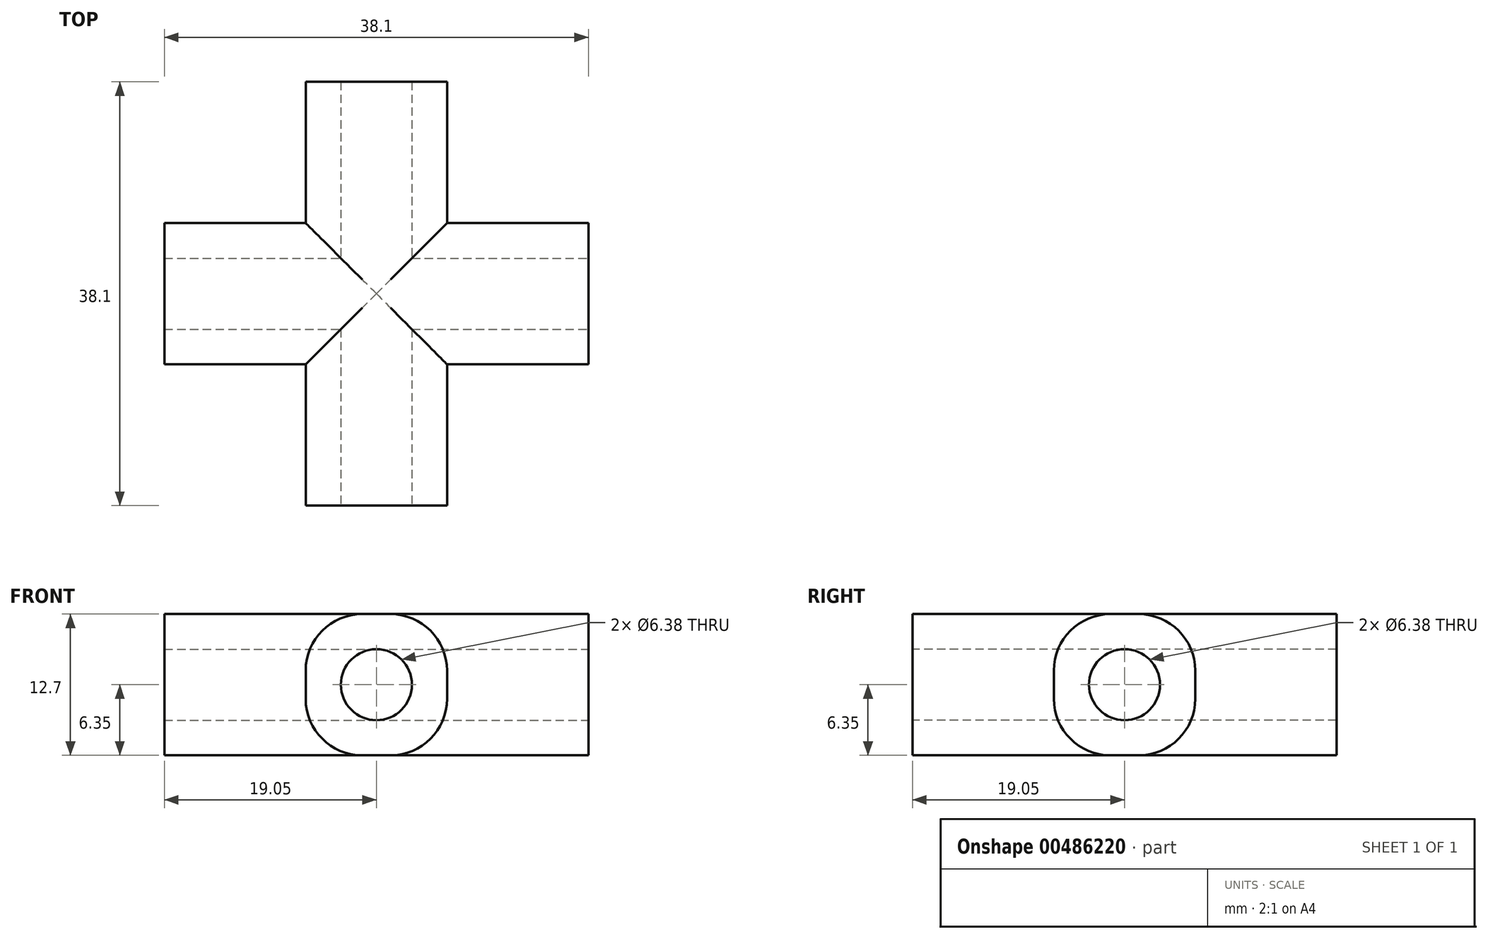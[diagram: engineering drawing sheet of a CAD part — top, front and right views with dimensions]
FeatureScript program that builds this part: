
annotation { "Feature Type Name" : "Feature", "Feature Type Description" : "" }
export const myFeature = defineFeature(function(context is Context, id is Id, definition is map)
    precondition{}
    {
        {
            var Q0;
            Q0=qCreatedBy(makeId("Top.planeOp"),FACE);
            var sketch = newSketch(context, id + "F0", { "sketchPlane" : qUnion([Q0])});
            skLineSegment(sketch, "E0.bottom", {"start": v(6.35, 19.05) * mm, "end": v(-6.35, 19.05) * mm});
            skLineSegment(sketch, "E0.top", {"start": v(6.35, -19.05) * mm, "end": v(-6.35, -19.05) * mm});
            skLineSegment(sketch, "E0.left", {"start": v(6.35, 19.05) * mm, "end": v(6.35, -19.05) * mm});
            skLineSegment(sketch, "E0.right", {"start": v(-6.35, 19.05) * mm, "end": v(-6.35, -19.05) * mm});
            skPoint(sketch, "E0.middle", {"position": v(0, 0) * mm});
            skLineSegment(sketch, "E1.bottom", {"start": v(19.05, 6.35) * mm, "end": v(-19.05, 6.35) * mm});
            skLineSegment(sketch, "E1.top", {"start": v(19.05, -6.35) * mm, "end": v(-19.05, -6.35) * mm});
            skLineSegment(sketch, "E1.left", {"start": v(19.05, 6.35) * mm, "end": v(19.05, -6.35) * mm});
            skLineSegment(sketch, "E1.right", {"start": v(-19.05, 6.35) * mm, "end": v(-19.05, -6.35) * mm});
            skSolve(sketch);
        }
        {
            var Q0;
            Q0 = qSketchRegion(id + "F0", true);
            extrude(context, id + "F1", {"entities" : qUnion([Q0]), "depth" : 12.7 * mm, "offsetDistance" : 25.4 * mm});
        }
        {
            var Q0;
            Q0=makeQuery(id+"F1.opExtrude","SWEPT_FACE",FACE,{"disambiguationData":[OSD([sQuery(id+"F0.wireOp",EDGE,"E1.left")])]});
            var sketch = newSketch(context, id + "F2", { "sketchPlane" : qUnion([Q0])});
            skLineSegment(sketch, "E2", {"start": v(0, 12.7) * mm, "end": v(0, 0) * mm});
            skCircle(sketch, "E3", {"center": v(0, 6.35) * mm, "radius": 3.19 * mm});
            skSolve(sketch);
        }
        {
            var Q0;
            Q0=makeQuery(id+"F1.opExtrude","SWEPT_FACE",FACE,{"disambiguationData":[OSD([sQuery(id+"F0.wireOp",EDGE,"E0.top")])]});
            var sketch = newSketch(context, id + "F3", { "sketchPlane" : qUnion([Q0])});
            skLineSegment(sketch, "E4", {"start": v(0, 12.7) * mm, "end": v(0, 0) * mm, "construction": true});
            skCircle(sketch, "E5", {"center": v(0, 6.35) * mm, "radius": 3.19 * mm});
            skSolve(sketch);
        }
        {
            var Q0;
            {var subQ0=sQuery(id+"F2.wireOp",EDGE,"E3");var subQ1=sQuery(id+"F2.wireOp",EDGE,"E2");var subQ2=makeQuery(id+"F2.imprint","INTERSECT",VERTEX,{"disambiguationData":[OD(0.0)],"derivedFrom":[subQ1,subQ0]});Q0=makeQuery(id+"F2.imprint","IMPRINT",FACE,{"disambiguationData":[TD([[makeQuery(id+"F2.imprint","IMPRINT",EDGE,{"disambiguationData":[TD([[subQ2,-1.0]])],"derivedFrom":subQ1}),-1.0]])]});}
            var Q1;
            {var subQ0=sQuery(id+"F2.wireOp",EDGE,"E3");var subQ1=sQuery(id+"F2.wireOp",EDGE,"E2");var subQ2=makeQuery(id+"F2.imprint","INTERSECT",VERTEX,{"disambiguationData":[OD(0.0)],"derivedFrom":[subQ1,subQ0]});Q1=makeQuery(id+"F2.imprint","IMPRINT",FACE,{"disambiguationData":[TD([[makeQuery(id+"F2.imprint","IMPRINT",EDGE,{"disambiguationData":[TD([[subQ2,-1.0]])],"derivedFrom":subQ1}),1.0]])]});}
            extrude(context, id + "F4", {"entities" : qUnion([Q0, Q1]), "operationType" : NewBodyOperationType.REMOVE, "oppositeDirection" : true, "depth" : 50.8 * mm, "offsetDistance" : 25.4 * mm});
        }
        {
            var Q0;
            Q0=makeQuery(id+"F3.imprint","IMPRINT",FACE,{"disambiguationData":[TD([[makeQuery(id+"F3.imprint","IMPRINT",EDGE,{"derivedFrom":sQuery(id+"F3.wireOp",EDGE,"E5")}),1.0]])]});
            extrude(context, id + "F5", {"entities" : qUnion([Q0]), "operationType" : NewBodyOperationType.REMOVE, "oppositeDirection" : true, "depth" : 76.2 * mm, "offsetDistance" : 25.4 * mm});
        }
        {
            var Q0;
            {var subQ0=sQuery(id+"F0.wireOp",EDGE,"E0.right");Q0=makeQuery(id+"F1.opExtrude","CAP_EDGE",EDGE,{"disambiguationData":[OSD([subQ0]),TDD([makeQuery(id+"F0.imprint","IMPRINT",EDGE,{"disambiguationData":[TD([[makeQuery(id+"F0.imprint","INTERSECT",VERTEX,{"derivedFrom":[sQuery(id+"F0.wireOp",EDGE,"E0.top"),subQ0]}),1.0]])],"derivedFrom":subQ0})])],"isStart":true});}
            var Q1;
            {var subQ0=sQuery(id+"F0.wireOp",EDGE,"E0.left");Q1=makeQuery(id+"F1.opExtrude","CAP_EDGE",EDGE,{"disambiguationData":[OSD([subQ0]),TDD([makeQuery(id+"F0.imprint","IMPRINT",EDGE,{"disambiguationData":[TD([[makeQuery(id+"F0.imprint","INTERSECT",VERTEX,{"derivedFrom":[sQuery(id+"F0.wireOp",EDGE,"E0.top"),subQ0]}),1.0]])],"derivedFrom":subQ0})])],"isStart":true});}
            var Q2;
            {var subQ0=sQuery(id+"F0.wireOp",EDGE,"E1.top");Q2=makeQuery(id+"F1.opExtrude","CAP_EDGE",EDGE,{"disambiguationData":[OSD([subQ0]),TDD([makeQuery(id+"F0.imprint","IMPRINT",EDGE,{"disambiguationData":[TD([[makeQuery(id+"F0.imprint","INTERSECT",VERTEX,{"derivedFrom":[subQ0,sQuery(id+"F0.wireOp",EDGE,"E1.left")]}),-1.0]])],"derivedFrom":subQ0})])],"isStart":true});}
            var Q3;
            {var subQ0=sQuery(id+"F0.wireOp",EDGE,"E1.bottom");Q3=makeQuery(id+"F1.opExtrude","CAP_EDGE",EDGE,{"disambiguationData":[OSD([subQ0]),TDD([makeQuery(id+"F0.imprint","IMPRINT",EDGE,{"disambiguationData":[TD([[makeQuery(id+"F0.imprint","INTERSECT",VERTEX,{"derivedFrom":[subQ0,sQuery(id+"F0.wireOp",EDGE,"E1.left")]}),-1.0]])],"derivedFrom":subQ0})])],"isStart":true});}
            var Q4;
            {var subQ0=sQuery(id+"F0.wireOp",EDGE,"E0.left");Q4=makeQuery(id+"F1.opExtrude","CAP_EDGE",EDGE,{"disambiguationData":[OSD([subQ0]),TDD([makeQuery(id+"F0.imprint","IMPRINT",EDGE,{"disambiguationData":[TD([[makeQuery(id+"F0.imprint","INTERSECT",VERTEX,{"derivedFrom":[sQuery(id+"F0.wireOp",EDGE,"E0.bottom"),subQ0]}),-1.0]])],"derivedFrom":subQ0})])],"isStart":true});}
            var Q5;
            {var subQ0=sQuery(id+"F0.wireOp",EDGE,"E0.right");Q5=makeQuery(id+"F1.opExtrude","CAP_EDGE",EDGE,{"disambiguationData":[OSD([subQ0]),TDD([makeQuery(id+"F0.imprint","IMPRINT",EDGE,{"disambiguationData":[TD([[makeQuery(id+"F0.imprint","INTERSECT",VERTEX,{"derivedFrom":[sQuery(id+"F0.wireOp",EDGE,"E0.bottom"),subQ0]}),-1.0]])],"derivedFrom":subQ0})])],"isStart":true});}
            var Q6;
            {var subQ0=sQuery(id+"F0.wireOp",EDGE,"E1.top");Q6=makeQuery(id+"F1.opExtrude","CAP_EDGE",EDGE,{"disambiguationData":[OSD([subQ0]),TDD([makeQuery(id+"F0.imprint","IMPRINT",EDGE,{"disambiguationData":[TD([[makeQuery(id+"F0.imprint","INTERSECT",VERTEX,{"derivedFrom":[subQ0,sQuery(id+"F0.wireOp",EDGE,"E1.right")]}),1.0]])],"derivedFrom":subQ0})])],"isStart":true});}
            var Q7;
            {var subQ0=sQuery(id+"F0.wireOp",EDGE,"E1.bottom");Q7=makeQuery(id+"F1.opExtrude","CAP_EDGE",EDGE,{"disambiguationData":[OSD([subQ0]),TDD([makeQuery(id+"F0.imprint","IMPRINT",EDGE,{"disambiguationData":[TD([[makeQuery(id+"F0.imprint","INTERSECT",VERTEX,{"derivedFrom":[subQ0,sQuery(id+"F0.wireOp",EDGE,"E1.right")]}),1.0]])],"derivedFrom":subQ0})])],"isStart":true});}
            var Q8;
            {var subQ0=sQuery(id+"F0.wireOp",EDGE,"E1.top");Q8=makeQuery(id+"F1.opExtrude","CAP_EDGE",EDGE,{"disambiguationData":[OSD([subQ0]),TDD([makeQuery(id+"F0.imprint","IMPRINT",EDGE,{"disambiguationData":[TD([[makeQuery(id+"F0.imprint","INTERSECT",VERTEX,{"derivedFrom":[subQ0,sQuery(id+"F0.wireOp",EDGE,"E1.right")]}),1.0]])],"derivedFrom":subQ0})])],"isStart":false});}
            var Q9;
            {var subQ0=sQuery(id+"F0.wireOp",EDGE,"E0.right");Q9=makeQuery(id+"F1.opExtrude","CAP_EDGE",EDGE,{"disambiguationData":[OSD([subQ0]),TDD([makeQuery(id+"F0.imprint","IMPRINT",EDGE,{"disambiguationData":[TD([[makeQuery(id+"F0.imprint","INTERSECT",VERTEX,{"derivedFrom":[sQuery(id+"F0.wireOp",EDGE,"E0.top"),subQ0]}),1.0]])],"derivedFrom":subQ0})])],"isStart":false});}
            var Q10;
            {var subQ0=sQuery(id+"F0.wireOp",EDGE,"E1.top");Q10=makeQuery(id+"F1.opExtrude","CAP_EDGE",EDGE,{"disambiguationData":[OSD([subQ0]),TDD([makeQuery(id+"F0.imprint","IMPRINT",EDGE,{"disambiguationData":[TD([[makeQuery(id+"F0.imprint","INTERSECT",VERTEX,{"derivedFrom":[subQ0,sQuery(id+"F0.wireOp",EDGE,"E1.left")]}),-1.0]])],"derivedFrom":subQ0})])],"isStart":false});}
            var Q11;
            {var subQ0=sQuery(id+"F0.wireOp",EDGE,"E1.bottom");Q11=makeQuery(id+"F1.opExtrude","CAP_EDGE",EDGE,{"disambiguationData":[OSD([subQ0]),TDD([makeQuery(id+"F0.imprint","IMPRINT",EDGE,{"disambiguationData":[TD([[makeQuery(id+"F0.imprint","INTERSECT",VERTEX,{"derivedFrom":[subQ0,sQuery(id+"F0.wireOp",EDGE,"E1.right")]}),1.0]])],"derivedFrom":subQ0})])],"isStart":false});}
            var Q12;
            {var subQ0=sQuery(id+"F0.wireOp",EDGE,"E0.right");Q12=makeQuery(id+"F1.opExtrude","CAP_EDGE",EDGE,{"disambiguationData":[OSD([subQ0]),TDD([makeQuery(id+"F0.imprint","IMPRINT",EDGE,{"disambiguationData":[TD([[makeQuery(id+"F0.imprint","INTERSECT",VERTEX,{"derivedFrom":[sQuery(id+"F0.wireOp",EDGE,"E0.bottom"),subQ0]}),-1.0]])],"derivedFrom":subQ0})])],"isStart":false});}
            var Q13;
            {var subQ0=sQuery(id+"F0.wireOp",EDGE,"E0.left");Q13=makeQuery(id+"F1.opExtrude","CAP_EDGE",EDGE,{"disambiguationData":[OSD([subQ0]),TDD([makeQuery(id+"F0.imprint","IMPRINT",EDGE,{"disambiguationData":[TD([[makeQuery(id+"F0.imprint","INTERSECT",VERTEX,{"derivedFrom":[sQuery(id+"F0.wireOp",EDGE,"E0.bottom"),subQ0]}),-1.0]])],"derivedFrom":subQ0})])],"isStart":false});}
            var Q14;
            {var subQ0=sQuery(id+"F0.wireOp",EDGE,"E0.left");Q14=makeQuery(id+"F1.opExtrude","CAP_EDGE",EDGE,{"disambiguationData":[OSD([subQ0]),TDD([makeQuery(id+"F0.imprint","IMPRINT",EDGE,{"disambiguationData":[TD([[makeQuery(id+"F0.imprint","INTERSECT",VERTEX,{"derivedFrom":[sQuery(id+"F0.wireOp",EDGE,"E0.top"),subQ0]}),1.0]])],"derivedFrom":subQ0})])],"isStart":false});}
            var Q15;
            {var subQ0=sQuery(id+"F0.wireOp",EDGE,"E1.bottom");Q15=makeQuery(id+"F1.opExtrude","CAP_EDGE",EDGE,{"disambiguationData":[OSD([subQ0]),TDD([makeQuery(id+"F0.imprint","IMPRINT",EDGE,{"disambiguationData":[TD([[makeQuery(id+"F0.imprint","INTERSECT",VERTEX,{"derivedFrom":[subQ0,sQuery(id+"F0.wireOp",EDGE,"E1.left")]}),-1.0]])],"derivedFrom":subQ0})])],"isStart":false});}
            fillet(context, id + "F6", {"entities" : qUnion([Q0, Q1, Q2, Q3, Q4, Q5, Q6, Q7, Q8, Q9, Q10, Q11, Q12, Q13, Q14, Q15]), "tangentPropagation" : true, "radius" : 5.08 * mm, "defaultsChanged" : false, "vertexSettings" : [], "allowEdgeOverflow" : false});
        }
    });
